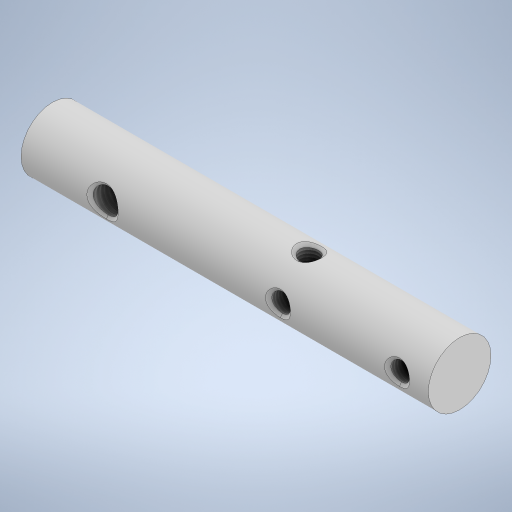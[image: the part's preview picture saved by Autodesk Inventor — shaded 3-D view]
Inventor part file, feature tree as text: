
AUTODESK INVENTOR PART (.ipt)
format: ipt  version: 2023 (Build 270158000, 158)  size: 345,088 bytes
history: native  units: mm
features: sketch x5, extrude x4, thread x4, other x1, chamfer x1, hole x1
ambient origin geometry x8: Origin, YZ Plane, XZ Plane, XY Plane, X Axis, Y Axis, Z Axis, Center Point
bodies: Body1 (feature_tree)
feature tree (16):
  other  "Твердое тело1"
  extrude  "Выдавливание1"  Depth=10.0mm
  extrude  "Выдавливание2"  Depth=65.0mm TaperAngle=0.0deg
  extrude  "Выдавливание3"  Depth=13.0mm
  thread  "Резьба1"
  thread  "Резьба2"
  extrude  "Выдавливание4"  Depth=4.0mm
  thread  "Резьба3"
  chamfer  "Фаска1"  Distance=18.0mm
  hole  "Отверстие1"  [1 undecoded]
  thread  "Резьба4"
  sketch  "Эскиз1"
  sketch  "Эскиз2"
  sketch  "Эскиз3"
  sketch  "Эскиз4"
  sketch  "Эскиз5"
note: 1 required parameter value undecoded (feature->parameter linkage not recoverable at this tier; creation-order binding heuristic only, values carry confidence <= 0.55)
